# Revit family: agtatec_Record_SldngDrset_THERMCORD-D-STA_WallBased
name_source: partatom
category: Doors
revit_build: Autodesk Revit Architecture 2015 (Build: 20140606_1530(x64)
units: mm (PartAtom-declared; Revit-internal decimal feet)

## types (8) — shared parameters
AccessoryOptions = Contact manufacturer
AlternativeDoorsetGlazing = Part of glazing spec
AntiFingerTrapRequirement = Yes
Assembly Code = B2030110
BIMObjectName = THERMCORD D-STA - Wall based.rfa
CenterOfDoor = 1246.00 mm
ClearHeightOfPassage = 2150.00 mm
ClearanceZones = No
Colour = Customer specific
Configuration = 1 or 2
Construction Type = Automatic Sliding Door
Description = Automatic Sliding Door
DoorIncluded = Yes
DoorOpening = 0.00 mm
DoorSeal = 1
DoorsetFasteners = Screws
DoorsetOperation = Automatic
DriveUnitExtraWidthLeft = 0.00 mm
DriveUnitExtraWidthRight = 0.00 mm
ElectronicLock = Yes
ExtraLeft = 0.00 mm
ExtraRight = 0.00 mm
ExtraWidthLeft = 0.00 mm
ExtraWidthRight = 0.00 mm
Finish = Powder coated, Anodized, customer specific
FireExit = No
FloorGuide = agtatec_Record_Sliding Door, Stainless Steel
FrameMaterial = Aluminium
FrameProfile = Aluminium
FrameSeal = Yes
Function = Interior
GlassLayers = 2
GlassThickness1 = 8.00 mm
GlassThickness2 = 0.00 mm
GlassType = Part of glazing spec
HandicapAccessible = Yes
HasDrive = Yes
IfcExportAs = IfcDoorStyle
IfcExportType = Door
InnerPanelWidth = 646.00 mm
InterlancingProfileHeight = 2195.00 mm
IsExternal = Yes
LeafColourOptions = All RAL, customer specific
Manufacturer = Record
ManufacturerURL = www.agta-record.com
Material = Aluminium
Model = Thermcord D-STA
ModelReference = Depends on the configuration
NominalLength = 0.00 mm
OffsetFromInteriorWallFace(OnlyApplicableForTypesWithTwoSidePanels) = 0.00 mm
OffsetFromWallSide = 0.00 mm
OffsetFromWallTop = 0.00 mm
Opening = 0.00 mm
OpeningAxis = 1246.00 mm
OpeningWidth = 1200.00 mm
OpeningWidthInWall = 1060.00 mm
Operation = Automatic
PanelFill = agtatec_Record_Sliding Door, Laminated Safety Glass (Clear)
PanelFrames = agtatec_Record_Sliding Door, Aluminium
PanelHeight = 2200.00 mm
ReferenceStandard = EN16005, EN16361, DIN 18650, etc.
ReplacementCost = Depends on the configuration and door type
Rough Width = 2498.00 mm
SelfClosing = Yes
ServiceLifeDuration = 10-15 years
Shape = Rectangular
SidePanelMinimumStandard = 646.00 mm
SidePanelWidthLeft = 646.00 mm
SidePanelWidthRight = 646.00 mm
SmokeStop = No
SupportLength = 2492.00 mm
Thickness = 0.00 mm
ThresholdRequired = Yes
ThresholdStripping = No additional required, part of the doorset
URL = www.agta-record.com
Uniclass2 = Ss_25_30_20_77
Version = Version 1.0
WallMountingProfile = No
WarrantyDescription = Depends on country
WarrantyDurationLabour = Depends on country
WarrantyDurationParts = Depends on country
WarrantyGuarantorLabour = Local door manufacturer
WarrantyGuarantorParts = Local door manufacturer
Weight = Depends on configuration and size
WithDriveCladding = Yes
WithinStandardSizes = Yes
WithoutDriveCladding(OnlyApplicableForTypesWithoutSidePanels) = No
zero-valued in all types: Cost, ThermalTransmittance

## per-type parameters (varying)
| type | DriveUnit | DriveUnitHeight | Height | InterlancingProfile1 | LeftPanel | NominalHeight | NominalWidth | RightPanel | Rough Height | SideVoidLeft | SideVoidRight | TotalHeight | TotalWidth | Width | WithSidePanels |
| THERMCORD D-STA 150mm drive unit height side panel left | agtatec_Record_Sliding Door, Stainless Steel | 150.00 mm | 2300.00 mm | No | Yes | 2300.00 mm | 1900.50 mm | No | 2306.00 mm | 646.00 mm | 70.00 mm | 2300.00 mm | 1900.50 mm | 1900.50 mm | No |
| THERMCORD D-STA 150mm drive unit height side panel right | agtatec_Record_Sliding Door, Sheet Metal (Painted Steel) | 150.00 mm | 2300.00 mm | No | No | 2300.00 mm | 1900.50 mm | Yes | 2306.00 mm | 70.00 mm | 646.00 mm | 2300.00 mm | 1900.50 mm | 1900.50 mm | No |
| THERMCORD D-STA 150mm drive unit height with two side panels | agtatec_Record_Sliding Door, Sheet Metal (Painted Steel) | 150.00 mm | 2300.00 mm | Yes | Yes | 2300.00 mm | 2492.00 mm | Yes | 2306.00 mm | 646.00 mm | 646.00 mm | 2300.00 mm | 2492.00 mm | 2492.00 mm | Yes |
| THERMCORD D-STA 150mm drive unit height without side panels | agtatec_Record_Sliding Door, Sheet Metal (Painted Steel) | 150.00 mm | 2300.00 mm | No | No | 2300.00 mm | 1309.00 mm | No | 2306.00 mm | 70.00 mm | 70.00 mm | 2300.00 mm | 1309.00 mm | 1309.00 mm | No |
| THERMCORD D-STA 200mm drive unit height side panel left | agtatec_Record_Sliding Door, Sheet Metal (Painted Steel) | 200.00 mm | 2350.00 mm | No | Yes | 2350.00 mm | 1900.50 mm | No | 2356.00 mm | 646.00 mm | 70.00 mm | 2350.00 mm | 1900.50 mm | 1900.50 mm | No |
| THERMCORD D-STA 200mm drive unit height side panel right | agtatec_Record_Sliding Door, Sheet Metal (Painted Steel) | 200.00 mm | 2350.00 mm | No | No | 2350.00 mm | 1900.50 mm | Yes | 2356.00 mm | 70.00 mm | 646.00 mm | 2350.00 mm | 1900.50 mm | 1900.50 mm | No |
| THERMCORD D-STA 200mm drive unit height with two side panels | agtatec_Record_Sliding Door, Sheet Metal (Painted Steel) | 200.00 mm | 2350.00 mm | Yes | Yes | 2350.00 mm | 2492.00 mm | Yes | 2356.00 mm | 646.00 mm | 646.00 mm | 2350.00 mm | 2492.00 mm | 2492.00 mm | Yes |
| THERMCORD D-STA 200mm drive unit height without side panels | agtatec_Record_Sliding Door, Sheet Metal (Painted Steel) | 200.00 mm | 2350.00 mm | No | No | 2350.00 mm | 1309.00 mm | No | 2356.00 mm | 70.00 mm | 70.00 mm | 2350.00 mm | 1309.00 mm | 1309.00 mm | No |

## geometry (parser evidence)
native form markers: Sweep x20
no freeform markers — native parametric forms only
